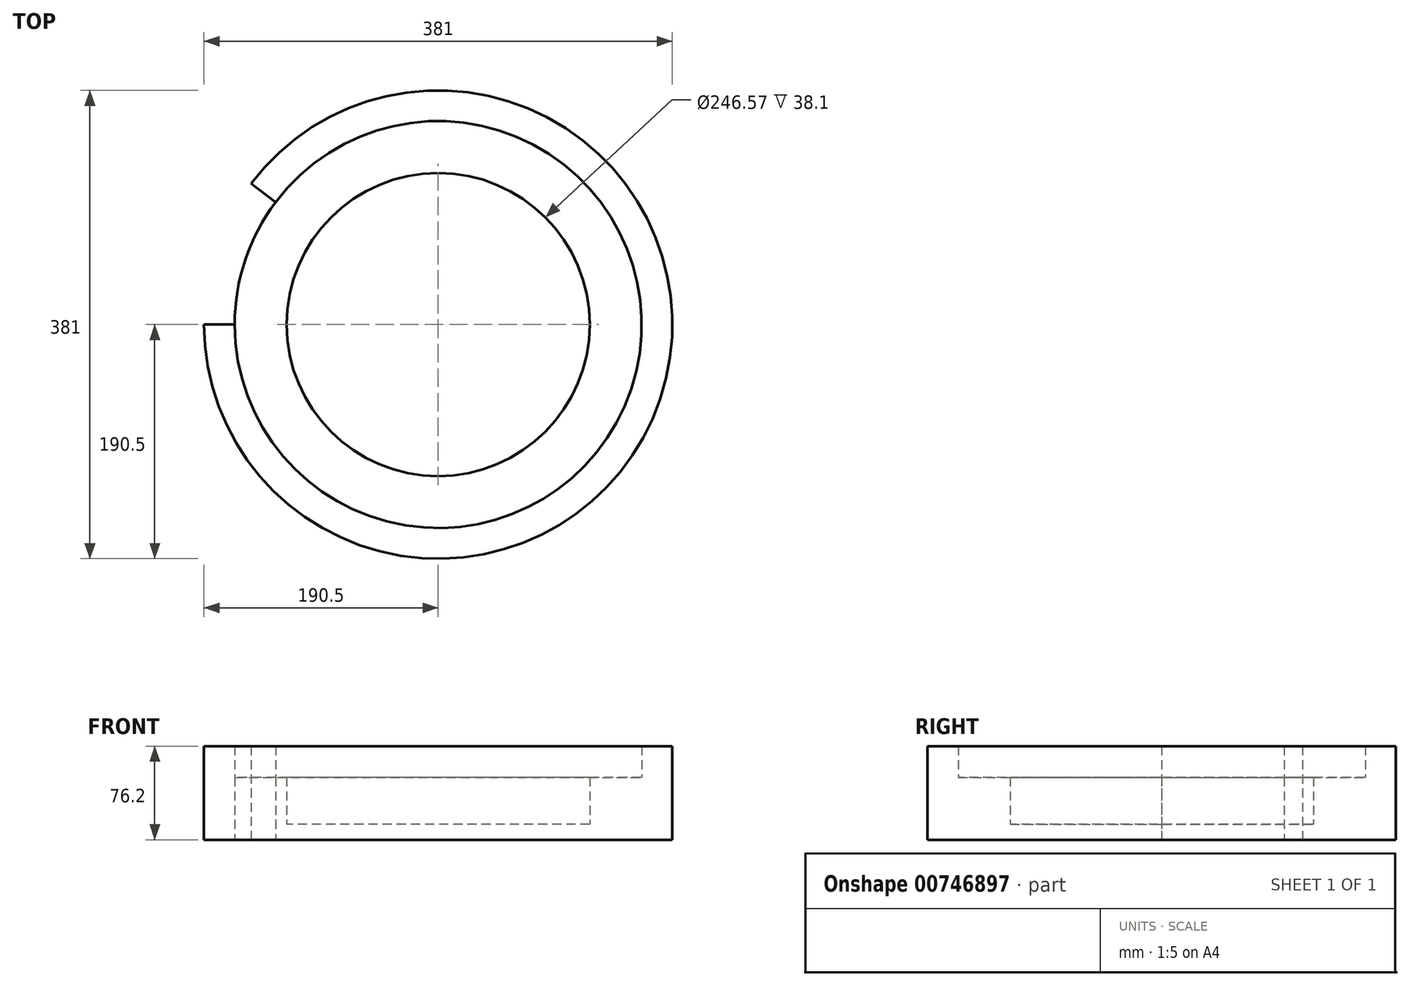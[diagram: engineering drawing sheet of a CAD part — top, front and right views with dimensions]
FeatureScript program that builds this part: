
annotation { "Feature Type Name" : "Feature", "Feature Type Description" : "" }
export const myFeature = defineFeature(function(context is Context, id is Id, definition is map)
    precondition{}
    {
        {
            var Q0;
            Q0=qCreatedBy(makeId("Top.planeOp"),FACE);
            var sketch = newSketch(context, id + "F0", { "sketchPlane" : qUnion([Q0])});
            skCircle(sketch, "E0", {"center": v(0, 0) * mm, "radius": 190.5 * mm});
            skCircle(sketch, "E1", {"center": v(0, 0) * mm, "radius": 165.55 * mm});
            skCircle(sketch, "E2", {"center": v(0, 0) * mm, "radius": 123.28 * mm});
            skLineSegment(sketch, "E3", {"start": v(0, 0) * mm, "end": v(-152.2, 114.57) * mm});
            skLineSegment(sketch, "E4", {"start": v(0, 0) * mm, "end": v(-190.5, 0) * mm});
            skSolve(sketch);
        }
        {
            var Q0;
            {var subQ0=sQuery(id+"F0.wireOp",EDGE,"E3");var subQ1=sQuery(id+"F0.wireOp",EDGE,"E0");var subQ2=makeQuery(id+"F0.imprint","INTERSECT",VERTEX,{"derivedFrom":[subQ1,subQ0]});Q0=makeQuery(id+"F0.imprint","IMPRINT",FACE,{"disambiguationData":[TD([[makeQuery(id+"F0.imprint","IMPRINT",EDGE,{"disambiguationData":[TD([[subQ2,1.0]])],"derivedFrom":subQ1}),1.0]])]});}
            extrude(context, id + "F1", {"entities" : qUnion([Q0]), "depth" : 76.2 * mm, "offsetDistance" : 25.4 * mm});
        }
        {
            var Q0;
            {var subQ0=sQuery(id+"F0.wireOp",EDGE,"E3");var subQ1=sQuery(id+"F0.wireOp",EDGE,"E1");var subQ2=makeQuery(id+"F0.imprint","INTERSECT",VERTEX,{"derivedFrom":[subQ1,subQ0]});Q0=makeQuery(id+"F0.imprint","IMPRINT",FACE,{"disambiguationData":[TD([[makeQuery(id+"F0.imprint","IMPRINT",EDGE,{"disambiguationData":[TD([[subQ2,1.0]])],"derivedFrom":subQ1}),1.0]])]});}
            extrude(context, id + "F2", {"entities" : qUnion([Q0]), "operationType" : NewBodyOperationType.ADD, "depth" : 50.8 * mm, "offsetDistance" : 25.4 * mm});
        }
        {
            var Q0;
            {var subQ0=sQuery(id+"F0.wireOp",EDGE,"E3");var subQ1=sQuery(id+"F0.wireOp",EDGE,"E2");var subQ2=makeQuery(id+"F0.imprint","INTERSECT",VERTEX,{"derivedFrom":[subQ1,subQ0]});Q0=makeQuery(id+"F0.imprint","IMPRINT",FACE,{"disambiguationData":[TD([[makeQuery(id+"F0.imprint","IMPRINT",EDGE,{"disambiguationData":[TD([[subQ2,1.0]])],"derivedFrom":subQ1}),1.0]])]});}
            extrude(context, id + "F3", {"entities" : qUnion([Q0]), "operationType" : NewBodyOperationType.ADD, "depth" : 12.7 * mm, "offsetDistance" : 25.4 * mm});
        }
        {
            var Q0;
            {var subQ0=sQuery(id+"F0.wireOp",EDGE,"E3");var subQ1=sQuery(id+"F0.wireOp",EDGE,"E1");var subQ2=makeQuery(id+"F0.imprint","INTERSECT",VERTEX,{"derivedFrom":[subQ1,subQ0]});Q0=makeQuery(id+"F0.imprint","IMPRINT",FACE,{"disambiguationData":[TD([[makeQuery(id+"F0.imprint","IMPRINT",EDGE,{"disambiguationData":[TD([[subQ2,-1.0]])],"derivedFrom":subQ1}),1.0]])]});}
            extrude(context, id + "F4", {"entities" : qUnion([Q0]), "operationType" : NewBodyOperationType.ADD, "depth" : 50.8 * mm, "offsetDistance" : 25.4 * mm});
        }
        {
            var Q0;
            {var subQ0=sQuery(id+"F0.wireOp",EDGE,"E3");var subQ1=sQuery(id+"F0.wireOp",EDGE,"E2");var subQ2=makeQuery(id+"F0.imprint","INTERSECT",VERTEX,{"derivedFrom":[subQ1,subQ0]});Q0=makeQuery(id+"F0.imprint","IMPRINT",FACE,{"disambiguationData":[TD([[makeQuery(id+"F0.imprint","IMPRINT",EDGE,{"disambiguationData":[TD([[subQ2,-1.0]])],"derivedFrom":subQ1}),1.0]])]});}
            extrude(context, id + "F5", {"entities" : qUnion([Q0]), "operationType" : NewBodyOperationType.ADD, "depth" : 12.7 * mm, "offsetDistance" : 25.4 * mm});
        }
    });
